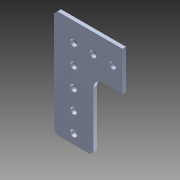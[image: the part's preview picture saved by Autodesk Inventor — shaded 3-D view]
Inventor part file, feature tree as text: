
AUTODESK INVENTOR PART (.ipt)
format: ipt  version: 2014 (Build 180170000, 170)  size: 142,336 bytes
history: native  units: in
note: dims shown in document units (in); Inventor stores cm internally (conversion verified against a paired STEP export)
features: other x2, extrude x1, imported_body x1, sketch x1
ambient origin geometry x8: Origin, YZ Plane, XZ Plane, XY Plane, X Axis, Y Axis, Z Axis, Center Point
bodies: Body1 (feature_tree)
feature tree (5):
  other  "Break-Corner1"
  other  "217-3548-STEP1"
  extrude  "Extrusion1"  Depth=1.0in TaperAngle=0.0deg
  imported_body  "Base1"
  sketch  "Sketch1"  dims[d0=1.0in d1=1.0in d2=0.0in]
